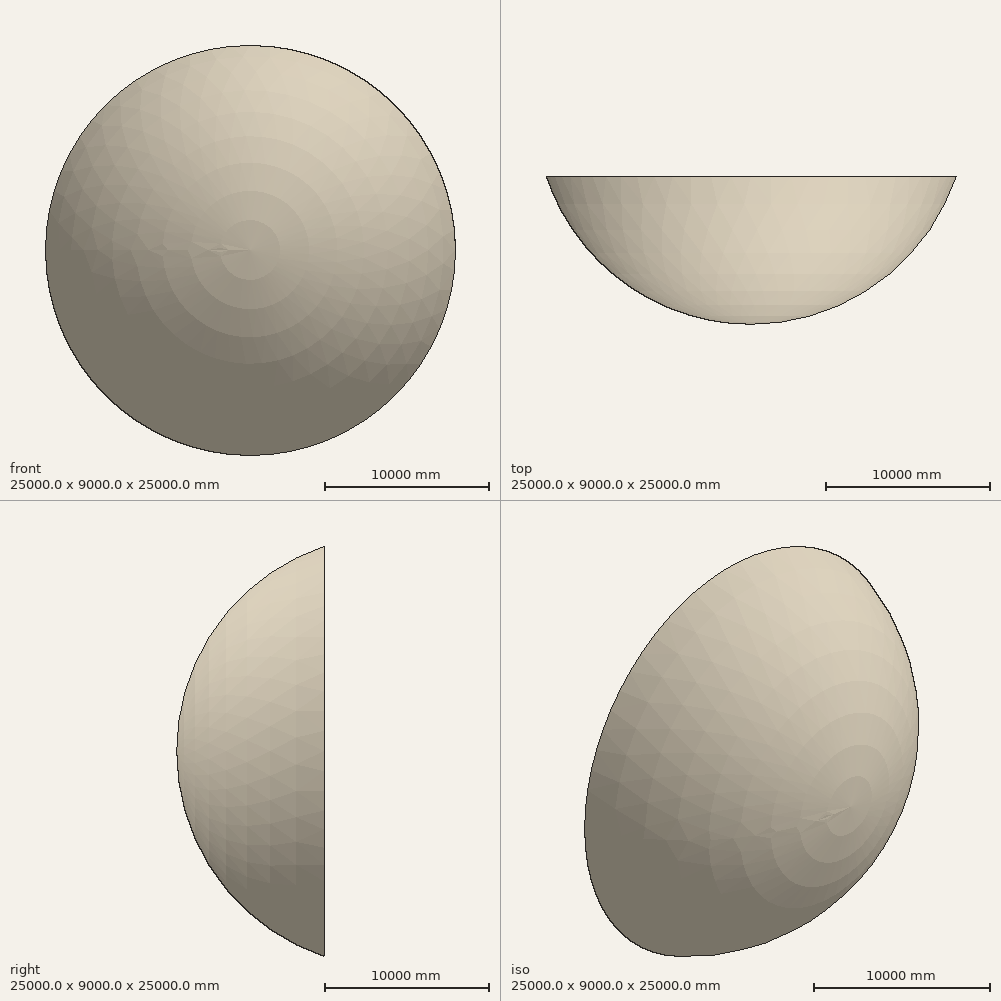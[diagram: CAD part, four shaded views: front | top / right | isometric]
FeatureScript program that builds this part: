
annotation { "Feature Type Name" : "Feature", "Feature Type Description" : "" }
export const myFeature = defineFeature(function(context is Context, id is Id, definition is map)
    precondition{}
    {
        {
            var Q0;
            Q0=qCreatedBy(makeId("Top.planeOp"),FACE);
            var sketch = newSketch(context, id + "F0", { "sketchPlane" : qUnion([Q0])});
            skLineSegment(sketch, "E0", {"start": v(-12500, 0) * mm, "end": v(0, 0) * mm, "construction": true});
            skLineSegment(sketch, "E1", {"start": v(0, 0) * mm, "end": v(0, -8500) * mm});
            skArc(sketch, "E2", {"start": v(-12500, 0) * mm, "mid": v(-7558.1, -6173.69) * mm, "end": v(0, -8500) * mm});
            skLineSegment(sketch, "E3", {"start": v(0, -9000) * mm, "end": v(0, -8500) * mm});
            skArc(sketch, "E4", {"start": v(-12500, 0) * mm, "mid": v(-7701.46, -6515.92) * mm, "end": v(0, -9000) * mm});
            skArc(sketch, "E5", {"start": v(0, -8500) * mm, "mid": v(7558.1, -6173.69) * mm, "end": v(12500, 0) * mm});
            skArc(sketch, "E6", {"start": v(0, -9000) * mm, "mid": v(7701.46, -6515.92) * mm, "end": v(12500, 0) * mm});
            skLineSegment(sketch, "E7", {"start": v(0, 0) * mm, "end": v(12500, 0) * mm});
            skSolve(sketch);
        }
        {
            var Q0;
            Q0=sQuery(id+"F0.wireOp",EDGE,"E5");
            var Q1;
            Q1=sQuery(id+"F0.wireOp",EDGE,"E6");
            var Q2;
            Q2=sQuery(id+"F0.wireOp",EDGE,"E1");
            revolve(context, id + "F1", {"bodyType" : ToolBodyType.SURFACE, "surfaceEntities" : qUnion([Q0, Q1]), "axis" : qUnion([Q2]), "revolveType" : RevolveType.FULL});
        }
        {
            var Q0;
            Q0=makeQuery(id+"F0.imprint","IMPRINT",FACE,{"disambiguationData":[TD([[makeQuery(id+"F0.imprint","IMPRINT",EDGE,{"derivedFrom":sQuery(id+"F0.wireOp",EDGE,"E1")}),1.0]])]});
            var Q1;
            Q1=makeQuery(id+"F0.imprint","IMPRINT",FACE,{"disambiguationData":[TD([[makeQuery(id+"F0.imprint","IMPRINT",EDGE,{"derivedFrom":sQuery(id+"F0.wireOp",EDGE,"E3")}),-1.0]])]});
            var Q2;
            Q2=sQuery(id+"F0.wireOp",EDGE,"E1");
            revolve(context, id + "F2", {"entities" : qUnion([Q0, Q1]), "axis" : qUnion([Q2]), "revolveType" : RevolveType.FULL});
        }
    });
